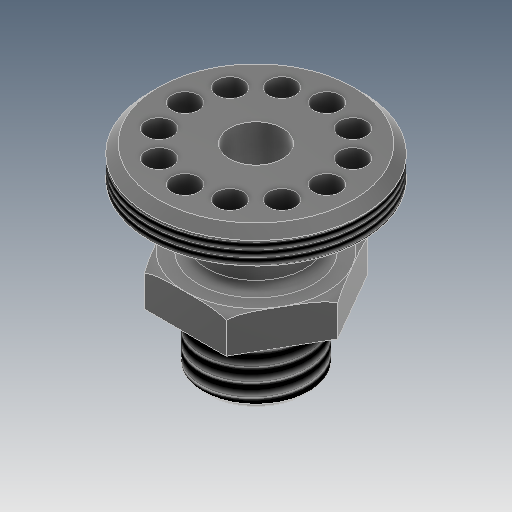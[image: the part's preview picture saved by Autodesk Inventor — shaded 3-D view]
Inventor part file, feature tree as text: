
AUTODESK INVENTOR PART (.ipt)
format: ipt  version: 2025 (Build 290162000, 162)  size: 280,576 bytes
history: native  units: mm
features: sketch x4, extrude x2, thread x2, revolve x1, fillet x1
ambient origin geometry x8: Origin, YZ Plane, XZ Plane, XY Plane, X Axis, Y Axis, Z Axis, Center Point
bodies: 实体1 (feature_tree)
feature tree (10):
  revolve  "旋转1"  [1 undecoded]
  fillet  "圆角1"  Radius=12.0mm
  extrude  "拉伸1"  Depth=24.0mm
  thread  "螺纹1"  [1 undecoded]
  thread  "螺纹2"  [1 undecoded]
  extrude  "拉伸2"  Depth=1.5mm
  sketch  "草图2"  dims[d6=1.0mm d7=18.45mm d8=11.0mm d9=24.0mm]
  sketch  "草图3"  dims[d10=45.0deg d11=1.5mm]
  sketch  "草图4"  dims[d12=2.0mm d13=7.0mm d14=8.0mm d15=22.0mm d16=15.0mm d17=1.5mm d18=360.0deg d19=2.0mm d20=10.0mm d21=0.0mm d22=20.0mm d23=0.0mm d24=20.0mm d25=0.0mm d26=6.0mm d27=16.0mm d28=120.0mm d30=360.0deg d32=10.0mm d33=0.0mm]
  sketch  "草图 - 环形阵列1"  dims[d1=48.0mm d2=12.0mm d3=5.0mm d4=22.0mm d0=6.0mm d5=12.0mm]
note: 3 required parameter values undecoded (feature->parameter linkage not recoverable at this tier; creation-order binding heuristic only, values carry confidence <= 0.55)